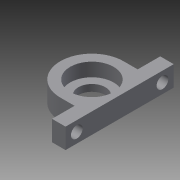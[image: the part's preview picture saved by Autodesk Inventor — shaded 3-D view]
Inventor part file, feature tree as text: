
AUTODESK INVENTOR PART (.ipt)
format: ipt  version: 2015 (Build 190159000, 159)  size: 112,640 bytes
history: native  units: in
note: dims shown in document units (in); Inventor stores cm internally (conversion verified against a paired STEP export)
features: extrude x3, sketch x2
ambient origin geometry x8: Origin, YZ Plane, XZ Plane, XY Plane, X Axis, Y Axis, Z Axis, Center Point
bodies: Solid1 (feature_tree)
feature tree (5):
  sketch  "Sketch1"  dims[d0=0.4843in d1=0.7598in]
  extrude  "Extrusion1"  Depth=0.4843in
  extrude  "Extrusion2"  Depth=1.1024in
  extrude  "Extrusion3"  Depth=0.3937in
  sketch  "Sketch2"  dims[d2=0.4724in d3=1.1024in d4=0.3937in d5=0.2362in d6=0.3937in d7=0.1181in d8=0.0in d9=0.3543in d10=0.0in d11=0.1969in d12=0.1969in d13=0.2047in d14=0.2047in d15=0.3543in d16=0.0in]
